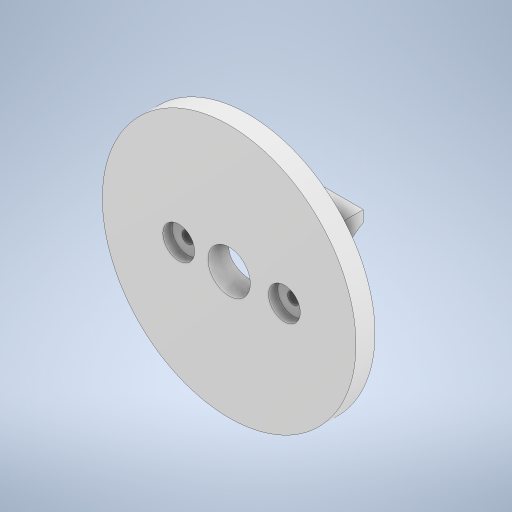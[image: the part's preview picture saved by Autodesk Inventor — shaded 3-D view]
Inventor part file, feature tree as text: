
AUTODESK INVENTOR PART (.ipt)
format: ipt  version: 2023 (Build 270158030, 158C)  size: 263,680 bytes
history: native  units: in
note: dims shown in document units (in); Inventor stores cm internally (conversion verified against a paired STEP export)
features: sketch x4, extrude x3, hole x1
ambient origin geometry x8: Origin, YZ Plane, XZ Plane, XY Plane, X Axis, Y Axis, Z Axis, Center Point
bodies: Solid1 (feature_tree)
feature tree (8):
  extrude  "Extrusion1"  Depth=2.5in
  extrude  "Extrusion2"  Depth=1.0in
  extrude  "Extrusion3"  Depth=4.7244in
  hole  "Hole1"  [1 undecoded]
  sketch  "Sketch1"  dims[d1=2.375in d3=2.5in]
  sketch  "Sketch2"  dims[d4=1.5748in d5=1.0in]
  sketch  "Sketch3"  dims[d6=3.0in d7=0.0in d8=4.7244in]
  sketch  "Sketch5"  dims[d9=0.3543in d10=0.0in d11=0.7874in d12=0.0in d13=0.0in d14=0.2165in d15=0.3389in d16=0.0246in d17=0.426in d18=0.5906in d19=0.1693in d20=90.0deg d21=0.3543in d22=0.8108in d23=1.9685in]
note: 1 required parameter value undecoded (feature->parameter linkage not recoverable at this tier; creation-order binding heuristic only, values carry confidence <= 0.55)
